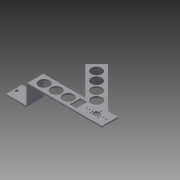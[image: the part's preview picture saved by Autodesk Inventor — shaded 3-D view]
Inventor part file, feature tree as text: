
AUTODESK INVENTOR PART (.ipt)
format: ipt  version: 2013 (Build 170138000, 138)  size: 295,936 bytes
history: native  units: in
note: dims shown in document units (in); Inventor stores cm internally (conversion verified against a paired STEP export)
features: sheet_metal_op x7, other x7, sketch x6
ambient origin geometry x8: Origin, YZ Plane, XZ Plane, XY Plane, X Axis, Y Axis, Z Axis, Center Point
bodies: Solid1 (feature_tree)
feature tree (20):
  sheet_metal_op  "Face1"
  sheet_metal_op  "Flange3"
  sheet_metal_op  "Flange4"
  sketch  "Sketch1"  dims[d5=3.0in]
  other  "Plate1"
  sketch  "Sketch4"  dims[d7=0.75in]
  other  "Plate4"
  sheet_metal_op  "Bend3"
  sheet_metal_op  "Corner3"
  sketch  "Sketch5"  dims[d8=0.125in]
  other  "Plate5"
  sheet_metal_op  "Bend4"
  sheet_metal_op  "Corner4"
  sketch  "Sketch6"  dims[d34=1.5in]
  sketch  "Sketch7"  dims[d35=1.5in]
  sketch  "Sketch8"  dims[d36=0.75in d37=0.75in d39=45.0deg d41=4.0in d42=4.0in d43=0.75in d44=1.25in d45=0.125in d46=0.0625in d47=0.25in d48=0.125in d49=2.0in d50=90.0deg d51=0.05in d52=0.5in d53=0.125in d54=0.125in d55=0.125in d56=0.0625in d57=0.25in d58=0.125in d59=2.0in d60=90.0deg d61=0.05in d62=0.5in d63=0.125in d64=0.125in d65=0.266in d66=0.266in d67=0.25in d68=0.75in d69=0.75in d70=0.25in d71=0.125in d72=0.0in d73=0.266in d74=0.266in d75=0.25in d76=0.75in d77=0.75in d78=0.25in d79=0.125in d80=0.0in d81=1.0in d82=1.0in d83=0.75in d84=0.75in d85=0.75in d86=0.75in d87=1.5748in d89=1.125in d90=0.3937in d92=1.0in d94=1.1811in d96=1.125in d97=0.3937in d99=1.0in d101=0.625in d102=0.625in d103=1.0in d104=0.25in d105=0.125in d106=0.0in]
  other  "Cut1"
  other  "Cut2"
  other  "Cut3"
  other  "Definition1"
